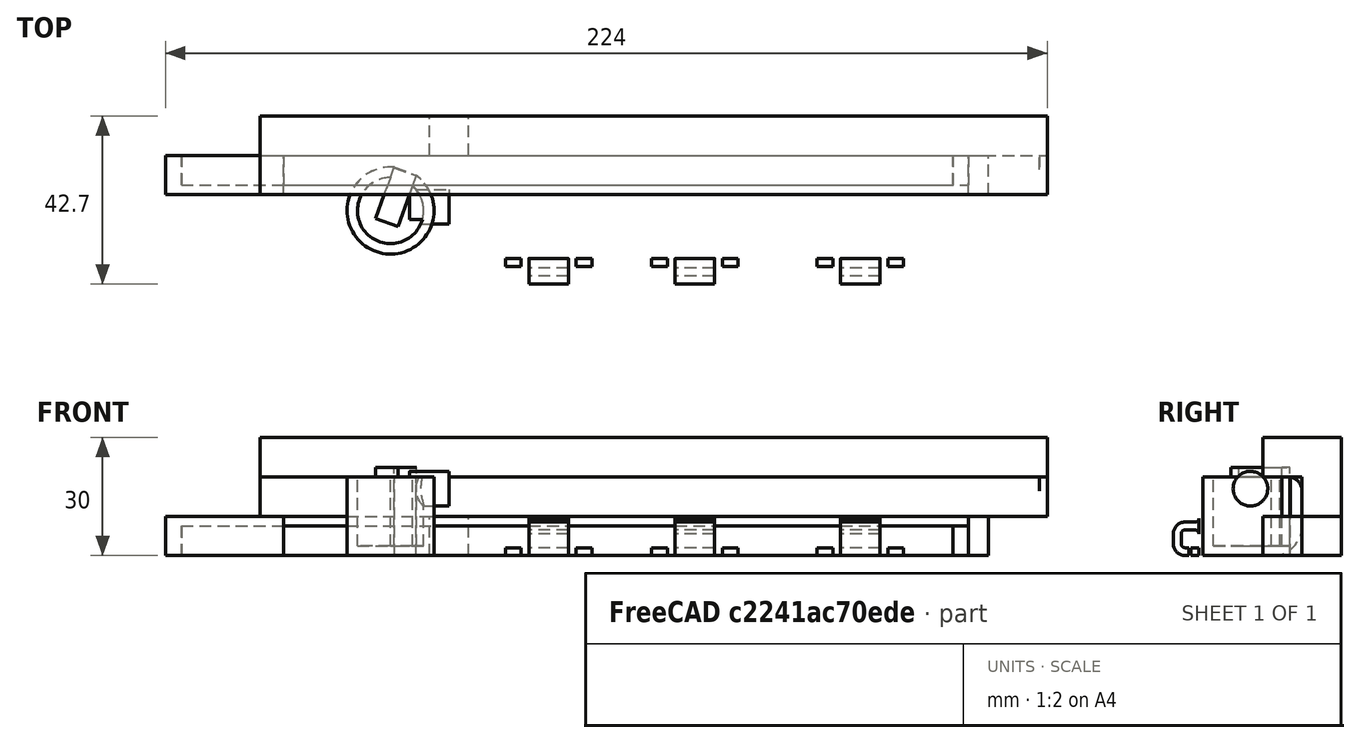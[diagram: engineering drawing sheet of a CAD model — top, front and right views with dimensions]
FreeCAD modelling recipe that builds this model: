
FCSTD DOCUMENT  (FreeCAD 0.19R0.19.2)
Label: v0_75
License: All rights reserved
LicenseURL: http://en.wikipedia.org/wiki/All_rights_reserved
objects: Part::Box×43, Part::Fillet×31, Part::MultiFuse×18, Part::Cut×13, Sketcher::SketchObject×11, Part::Extrusion×9, Part::Cylinder×6, App::MeasureDistance×5, Part::Revolution×1
note: 132 computed .brp shape members not serialized (recipe doc carries the construction recipe); baked Part::Feature solids carry a one-line shape summary decoded from their .brp

FEATURE [Sketcher::SketchObject] Sketch001
  FullyConstrained = true
  sketch-geometry (47):
    g0: Circle CenterX=-129.5 CenterY=-8 CenterZ=0 NormalX=0 NormalY=0 NormalZ=1 AngleXU=0 Radius=1
    g1: Circle CenterX=-129.5 CenterY=-3 CenterZ=0 NormalX=0 NormalY=0 NormalZ=1 AngleXU=0 Radius=1
    g2: Circle CenterX=-124.5 CenterY=-3 CenterZ=0 NormalX=0 NormalY=0 NormalZ=1 AngleXU=0 Radius=1
    g3: BSplineCurve PolesCount=3 KnotsCount=2 Degree=2 IsPeriodic=0
    g4: GeomPoint X=-129.5 Y=-8 Z=0
    g5: GeomPoint X=-124.5 Y=-3 Z=0
    g6: LineSegment StartX=18.6 StartY=-2.9 StartZ=0 EndX=23.6 EndY=-2.9 EndZ=0
    g7: ArcOfCircle CenterX=23.8 CenterY=-14.35 CenterZ=0 NormalX=0 NormalY=0 NormalZ=1 AngleXU=0 Radius=2.3 StartAngle=8e-16 EndAngle=1.5708
    g8: ArcOfCircle CenterX=23.8 CenterY=-18.1 CenterZ=0 NormalX=0 NormalY=0 NormalZ=1 AngleXU=0 Radius=2.3 StartAngle=4.71239 EndAngle=6.28319
    g9: LineSegment StartX=23.8 StartY=-20.4 StartZ=0 EndX=21.1 EndY=-20.4 EndZ=0
    g10: LineSegment StartX=21.1 StartY=-22.9 StartZ=0 EndX=21.1 EndY=-20.4 EndZ=0
    g11: LineSegment StartX=26.1 StartY=-14.35 StartZ=0 EndX=26.1 EndY=-18.1 EndZ=0
    g12: LineSegment StartX=18.6 StartY=-5.40742 StartZ=0 EndX=18.6 EndY=-2.9 EndZ=0
    g13: ArcOfCircle CenterX=18.8 CenterY=-8.1 CenterZ=0 NormalX=0 NormalY=0 NormalZ=1 AngleXU=0 Radius=2.7 StartAngle=1.64494 EndAngle=3.14159
    g14: ArcOfCircle CenterX=18.8 CenterY=-11.85 CenterZ=0 NormalX=0 NormalY=0 NormalZ=1 AngleXU=0 Radius=2.7 StartAngle=3.14159 EndAngle=4.71239
    g15: LineSegment StartX=16.1 StartY=-8.1 StartZ=0 EndX=16.1 EndY=-11.85 EndZ=0
    g16: LineSegment StartX=18.8 StartY=-14.55 StartZ=0 EndX=21.5 EndY=-14.55 EndZ=0
    g17: LineSegment StartX=21.5 StartY=-12.05 StartZ=0 EndX=21.5 EndY=-14.55 EndZ=0
    g18: LineSegment StartX=21.5 StartY=-12.05 StartZ=0 EndX=23.8 EndY=-12.05 EndZ=0
    g19: LineSegment StartX=16.1 StartY=-22.9 StartZ=0 EndX=21.1 EndY=-22.9 EndZ=0
    g20: LineSegment StartX=23.6 StartY=-2.9 StartZ=0 EndX=23.6 EndY=0 EndZ=0
    g21: LineSegment StartX=16.1 StartY=-22.9 StartZ=0 EndX=16.1 EndY=-26.2 EndZ=0
    g22: BSplineCurve PolesCount=3 KnotsCount=2 Degree=2 IsPeriodic=0
    g23: LineSegment StartX=2.6 StartY=-3 StartZ=0 EndX=-124.5 EndY=-3 EndZ=0
    g24: ArcOfCircle CenterX=-134.9 CenterY=-8.6 CenterZ=0 NormalX=0 NormalY=0 NormalZ=1 AngleXU=0 Radius=0.5 StartAngle=4.71238 EndAngle=6.28319
    g25: LineSegment StartX=-141.9 StartY=-9.1 StartZ=0 EndX=-134.9 EndY=-9.1 EndZ=0
    g26: LineSegment StartX=-141.9 StartY=-33.8 StartZ=0 EndX=-141.5 EndY=-33.8 EndZ=0
    g27: LineSegment StartX=-141.9 StartY=-9.1 StartZ=0 EndX=-141.9 EndY=-33.8 EndZ=0
    g28: LineSegment StartX=-134.4 StartY=-8.6 StartZ=0 EndX=-134.4 EndY=0 EndZ=0
    g29: LineSegment StartX=-134.4 StartY=0 StartZ=0 EndX=23.6 EndY=0 EndZ=0
    g30: LineSegment StartX=-133.5 StartY=-26.2 StartZ=0 EndX=16.1 EndY=-26.2 EndZ=0
    g31-g36: Circle x6 (B-spline internal-alignment scaffolding for g37; pole/knot coordinates omitted)
    g37: BSplineCurve PolesCount=6 KnotsCount=4 Degree=3 IsPeriodic=0
    g38-g41: GeomPoint x4 (B-spline internal-alignment scaffolding for g37; pole/knot coordinates omitted)
    g42: BSplineCurve PolesCount=3 KnotsCount=2 Degree=2 IsPeriodic=0
    g43: LineSegment StartX=-129.5 StartY=-8 StartZ=0 EndX=-129.5 EndY=-18.2 EndZ=0
    g44: BSplineCurve PolesCount=3 KnotsCount=2 Degree=2 IsPeriodic=0
    g45: LineSegment StartX=7.6 StartY=-8 StartZ=0 EndX=7.6 EndY=-18.2 EndZ=0
    g46: LineSegment StartX=2.6 StartY=-23.2 StartZ=0 EndX=-124.5 EndY=-23.2 EndZ=0
  constraints (87):
    c: Weight(g0) = 1
    c: Equal(g0,g1)
    c: Equal(g0,g2)
    c: InternalAlignment(g0,g3)
    c: InternalAlignment(g1,g3)
    c: InternalAlignment(g2,g3)
    c: InternalAlignment(g4,g3)
    c: InternalAlignment(g5,g3)
    c: Block(g3)
    c: Block(g8)
    c: Block(g7)
    c: Coincident(g9,g8)
    c: Horizontal(g9)
    c: Vertical(g10)
    c: Coincident(g10,g9)
    c: Coincident(g11,g7)
    c: Coincident(g11,g8)
    c: Vertical(g11)
    c: Vertical(g12)
    c: Block(g12)
    c: Coincident(g6,g12)
    c: Horizontal(g6)
    c: Block(g6)
    c: Coincident(g13,g12)
    c: Block(g14)
    c: Vertical(g15)
    c: Block(g15)
    c: Coincident(g16,g14)
    c: Horizontal(g16)
    c: Vertical(g17)
    c: Coincident(g17,g16)
    c: Block(g17)
    c: Coincident(g18,g7)
    c: Horizontal(g18)
    c: Block(g18)
    c: Coincident(g19,g10)
    c: Horizontal(g19)
    c: Block(g19)
    c: Block(g13)
    c: Coincident(g20,g6)
    c: Vertical(g20)
    c: Vertical(g21)
    c: Block(g21)
    c: Block(g22)
    c: Coincident(g23,g22)
    c: Coincident(g23,g3)
    c: Horizontal(g23)
    c: Block(g24)
    c: Coincident(g25,g24)
    c: Horizontal(g25)
    c: Horizontal(g26)
    c: Block(g26)
    c: Coincident(g27,g25)
    c: Coincident(g27,g26)
    c: Vertical(g27)
    c: Coincident(g28,g24)
    c: Vertical(g28)
    c: Coincident(g29,g28)
    c: Coincident(g29,g20)
    c: Horizontal(g29)
    c: Block(g29)
    c: Block(g25)
    c: Block(g28)
    c: Block(g27)
    c: Coincident(g30,g21)
    c: Horizontal(g30)
    c: Block(g30)
    c: Coincident(g37,g26)
    c: Weight(g31) = 1
    c: Equal(g31, g32-g36) x5
    c: Coincident(g37,g30)
    c: InternalAlignment(g31-g36 -> g37) x6
    c: InternalAlignment(g38-g41 -> g37) x4
    c: Block(g37)
    c: Block(g42)
    c: Coincident(g43,g3)
    c: Coincident(g43,g42)
    c: Vertical(g43)
    c: Distance(g43) = 10.2
    c: Block(g44)
    c: Coincident(g45,g22)
    c: Coincident(g45,g44)
    c: Vertical(g45)
    c: Distance(g45) = 10.2
    c: Coincident(g46,g44)
    c: Coincident(g46,g42)
    c: Horizontal(g46)
FEATURE [Part::Extrusion] Extrude001
  Base = -> Sketch001
  Dir = (0,0,1)
  DirMode = 2
  FaceMakerClass = Part::FaceMakerBullseye
  LengthFwd = 20
  LengthRev = 0
  Solid = true
  Symmetric = false
FEATURE [Sketcher::SketchObject] Sketch004
  FullyConstrained = true
  Placement = pos=(0,0,0) rot=(1,0,0;1.5708rad)
  sketch-geometry (12):
    g0: LineSegment StartX=15.75 StartY=2.5 StartZ=0 EndX=15.75 EndY=0 EndZ=0
    g1: Circle CenterX=15.75 CenterY=2.5 CenterZ=0 NormalX=0 NormalY=0 NormalZ=1 AngleXU=0 Radius=1
    g2: Circle CenterX=10.55 CenterY=2.5 CenterZ=0 NormalX=0 NormalY=0 NormalZ=1 AngleXU=0 Radius=1
    g3: Circle CenterX=10.55 CenterY=8 CenterZ=0 NormalX=0 NormalY=0 NormalZ=1 AngleXU=0 Radius=1
    g4: BSplineCurve PolesCount=3 KnotsCount=2 Degree=2 IsPeriodic=0
    g5: GeomPoint X=15.75 Y=2.5 Z=0
    g6: GeomPoint X=10.55 Y=8 Z=0
    g7: LineSegment StartX=1.9 StartY=8 StartZ=0 EndX=10.55 EndY=8 EndZ=0
    g8: LineSegment StartX=1.9 StartY=-2.4 StartZ=0 EndX=1.9 EndY=8 EndZ=0
    g9: LineSegment StartX=3.30092 StartY=-2.4 StartZ=0 EndX=3.30092 EndY=0 EndZ=0
    g10: LineSegment StartX=15.75 StartY=0 StartZ=0 EndX=3.30092 EndY=0 EndZ=0
    g11: LineSegment StartX=3.30092 StartY=-2.4 StartZ=0 EndX=1.9 EndY=-2.4 EndZ=0
  constraints (26):
    c: Vertical(g0)
    c: Distance(g0) = 2.5
    c: Coincident(g4,g0)
    c: Weight(g1) = 1
    c: Equal(g1,g2)
    c: Equal(g1,g3)
    c: InternalAlignment(g1,g4)
    c: InternalAlignment(g2,g4)
    c: InternalAlignment(g3,g4)
    c: InternalAlignment(g5,g4)
    c: InternalAlignment(g6,g4)
    c: Block(g4)
    c: Coincident(g7,g4)
    c: Horizontal(g7)
    c: Vertical(g8)
    c: Coincident(g8,g7)
    c: Block(g8)
    c: Vertical(g9)
    c: Coincident(g10,g0)
    c: PointOnObject(g10,g-1)
    c: Horizontal(g10)
    c: Coincident(g10,g9)
    c: Block(g9)
    c: Coincident(g11,g9)
    c: Coincident(g11,g8)
    c: Horizontal(g11)
FEATURE [Part::Revolution] Revolve  label="mainScrewStandRevolve"
  Angle = 360
  Axis = (0,0,1)
  Base = (0,0,0)
  FaceMakerClass = Part::FaceMakerBullseye
  Placement = pos=(-101.95,-15.3,0) rot=(0,0,1;0rad)
  Solid = true
  Source = -> Sketch004
  Symmetric = false
FEATURE [Sketcher::SketchObject] Sketch044
  FullyConstrained = true
  MapMode = 4
  Placement = pos=(0,0,0) rot=(0.57735,0.57735,0.57735;2.0944rad)
  sketch-geometry (14):
    g0: LineSegment StartX=6.08745 StartY=-4.11588 StartZ=0 EndX=6.08745 EndY=-2.11589 EndZ=0
    g1: LineSegment StartX=8.08745 StartY=1.38411 StartZ=0 EndX=8.08745 EndY=-1.11589 EndZ=0
    g2: ArcOfCircle CenterX=7.08745 CenterY=-1.11589 CenterZ=0 NormalX=0 NormalY=0 NormalZ=1 AngleXU=0 Radius=1 StartAngle=4.71239 EndAngle=6.28319
    g3: LineSegment StartX=6.08745 StartY=-2.11589 StartZ=0 EndX=7.08745 EndY=-2.11589 EndZ=0
    g4: LineSegment StartX=6.08745 StartY=-4.11588 StartZ=0 EndX=7.08745 EndY=-4.11588 EndZ=0
    g5: ArcOfCircle CenterX=7.08745 CenterY=-1.11589 CenterZ=0 NormalX=0 NormalY=0 NormalZ=1 AngleXU=0 Radius=3 StartAngle=4.71239 EndAngle=6.28319
    g6: ArcOfCircle CenterX=7.08745 CenterY=1.38411 CenterZ=0 NormalX=0 NormalY=0 NormalZ=1 AngleXU=0 Radius=1 StartAngle=5.35e-14 EndAngle=1.5708
    g7: LineSegment StartX=10.0875 StartY=-1.11588 StartZ=0 EndX=10.0875 EndY=1.38411 EndZ=0
    g8: ArcOfCircle CenterX=7.08745 CenterY=1.38411 CenterZ=0 NormalX=0 NormalY=0 NormalZ=1 AngleXU=0 Radius=3 StartAngle=3.57e-14 EndAngle=1.5708
    g9: ArcOfCircle CenterX=4.58745 CenterY=1.38412 CenterZ=0 NormalX=0 NormalY=0 NormalZ=1 AngleXU=0 Radius=1 StartAngle=1.57081 EndAngle=3.14159
    g10: LineSegment StartX=4.58744 StartY=2.38411 StartZ=0 EndX=7.08745 EndY=2.38411 EndZ=0
    g11: LineSegment StartX=4.58745 StartY=4.38411 StartZ=0 EndX=7.08745 EndY=4.38411 EndZ=0
    g12: ArcOfCircle CenterX=4.58745 CenterY=5.38411 CenterZ=0 NormalX=0 NormalY=0 NormalZ=1 AngleXU=0 Radius=1 StartAngle=3.14159 EndAngle=4.71239
    g13: LineSegment StartX=3.58745 StartY=5.38411 StartZ=0 EndX=3.58745 EndY=1.38411 EndZ=0
  constraints (33):
    c: Vertical(g0)
    c: Block(g0)
    c: Block(g1)
    c: Coincident(g2,g1)
    c: Coincident(g3,g0)
    c: Coincident(g3,g2)
    c: Horizontal(g3)
    c: Block(g2)
    c: Coincident(g4,g0)
    c: Horizontal(g4)
    c: Coincident(g5,g2)
    c: Block(g5)
    c: Block(g4)
    c: Coincident(g6,g1)
    c: Block(g6)
    c: Coincident(g7,g5)
    c: Vertical(g7)
    c: Coincident(g8,g6)
    c: Block(g8)
    c: Block(g7)
    c: Coincident(g10,g9)
    c: Coincident(g10,g6)
    c: Horizontal(g10)
    c: Block(g10)
    c: Block(g9)
    c: Coincident(g11,g8)
    c: Horizontal(g11)
    c: Block(g12)
    c: Block(g11)
    c: Coincident(g13,g12)
    c: Coincident(g13,g9)
    c: Vertical(g13)
    c: Tangent(g13,g9)
FEATURE [Sketcher::SketchObject] Sketch045
  FullyConstrained = true
  MapMode = 4
  Placement = pos=(0,0,0) rot=(0.57735,0.57735,0.57735;2.0944rad)
  sketch-geometry (14):
    g0: LineSegment StartX=6.08745 StartY=-4.11588 StartZ=0 EndX=6.08745 EndY=-2.11589 EndZ=0
    g1: LineSegment StartX=8.08745 StartY=1.38411 StartZ=0 EndX=8.08745 EndY=-1.11589 EndZ=0
    g2: ArcOfCircle CenterX=7.08745 CenterY=-1.11589 CenterZ=0 NormalX=0 NormalY=0 NormalZ=1 AngleXU=0 Radius=1 StartAngle=4.71239 EndAngle=6.28319
    g3: LineSegment StartX=6.08745 StartY=-2.11589 StartZ=0 EndX=7.08745 EndY=-2.11589 EndZ=0
    g4: LineSegment StartX=6.08745 StartY=-4.11588 StartZ=0 EndX=7.08745 EndY=-4.11588 EndZ=0
    g5: ArcOfCircle CenterX=7.08745 CenterY=-1.11589 CenterZ=0 NormalX=0 NormalY=0 NormalZ=1 AngleXU=0 Radius=3 StartAngle=4.71239 EndAngle=6.28319
    g6: ArcOfCircle CenterX=7.08745 CenterY=1.38411 CenterZ=0 NormalX=0 NormalY=0 NormalZ=1 AngleXU=0 Radius=1 StartAngle=5.35e-14 EndAngle=1.5708
    g7: LineSegment StartX=10.0875 StartY=-1.11588 StartZ=0 EndX=10.0875 EndY=1.38411 EndZ=0
    g8: ArcOfCircle CenterX=7.08745 CenterY=1.38411 CenterZ=0 NormalX=0 NormalY=0 NormalZ=1 AngleXU=0 Radius=3 StartAngle=3.57e-14 EndAngle=1.5708
    g9: ArcOfCircle CenterX=4.58745 CenterY=1.38412 CenterZ=0 NormalX=0 NormalY=0 NormalZ=1 AngleXU=0 Radius=1 StartAngle=1.57081 EndAngle=3.14159
    g10: LineSegment StartX=4.58744 StartY=2.38411 StartZ=0 EndX=7.08745 EndY=2.38411 EndZ=0
    g11: LineSegment StartX=4.58745 StartY=4.38411 StartZ=0 EndX=7.08745 EndY=4.38411 EndZ=0
    g12: ArcOfCircle CenterX=4.58745 CenterY=5.38411 CenterZ=0 NormalX=0 NormalY=0 NormalZ=1 AngleXU=0 Radius=1 StartAngle=3.14159 EndAngle=4.71239
    g13: LineSegment StartX=3.58745 StartY=5.38411 StartZ=0 EndX=3.58745 EndY=1.38411 EndZ=0
  constraints (33):
    c: Vertical(g0)
    c: Block(g0)
    c: Block(g1)
    c: Coincident(g2,g1)
    c: Coincident(g3,g0)
    c: Coincident(g3,g2)
    c: Horizontal(g3)
    c: Block(g2)
    c: Coincident(g4,g0)
    c: Horizontal(g4)
    c: Coincident(g5,g2)
    c: Block(g5)
    c: Block(g4)
    c: Coincident(g6,g1)
    c: Block(g6)
    c: Coincident(g7,g5)
    c: Vertical(g7)
    c: Coincident(g8,g6)
    c: Block(g8)
    c: Block(g7)
    c: Coincident(g10,g9)
    c: Coincident(g10,g6)
    c: Horizontal(g10)
    c: Block(g10)
    c: Block(g9)
    c: Coincident(g11,g8)
    c: Horizontal(g11)
    c: Block(g12)
    c: Block(g11)
    c: Coincident(g13,g12)
    c: Coincident(g13,g9)
    c: Vertical(g13)
    c: Tangent(g13,g9)
FEATURE [Part::Extrusion] Extrude040
  Base = -> Sketch045
  Dir = (1,0,0)
  DirMode = 2
  FaceMakerClass = Part::FaceMakerBullseye
  LengthFwd = 10
  LengthRev = 0
  Placement = pos=(-71.7,-22.61,4.115) rot=(0,0,1;3.14159rad)
  Solid = true
  Symmetric = false
FEATURE [Part::Box] Box017  label="Cube017"
  AttacherType = Attacher::AttachEngine3D
  Height = 2
  Length = 2
  Placement = pos=(-85.7,-21.3,0) rot=(0,0,1;0rad)
  Width = 2
FEATURE [Part::Box] Box018  label="Cube018"
  AttacherType = Attacher::AttachEngine3D
  Height = 2
  Length = 2
  Placement = pos=(-87.7,-21.3,0) rot=(0,0,1;0rad)
  Width = 2
FEATURE [Part::MultiFuse] Fusion
  Placement = pos=(0,-6.9,0) rot=(0,0,1;0rad)
  Shapes = -> [Box017,Box018]
FEATURE [Part::Box] Box  label="Cube"
  AttacherType = Attacher::AttachEngine3D
  Height = 10
  Length = 10
  Placement = pos=(-107,0,0) rot=(0,0,1;0rad)
  Width = 10
FEATURE [Sketcher::SketchObject] Sketch046
  FullyConstrained = true
  MapMode = 4
  Placement = pos=(0,0,0) rot=(0.57735,0.57735,0.57735;2.0944rad)
  sketch-geometry (14):
    g0: LineSegment StartX=6.08745 StartY=-4.11588 StartZ=0 EndX=6.08745 EndY=-2.11589 EndZ=0
    g1: LineSegment StartX=8.08745 StartY=1.38411 StartZ=0 EndX=8.08745 EndY=-1.11589 EndZ=0
    g2: ArcOfCircle CenterX=7.08745 CenterY=-1.11589 CenterZ=0 NormalX=0 NormalY=0 NormalZ=1 AngleXU=0 Radius=1 StartAngle=4.71239 EndAngle=6.28319
    g3: LineSegment StartX=6.08745 StartY=-2.11589 StartZ=0 EndX=7.08745 EndY=-2.11589 EndZ=0
    g4: LineSegment StartX=6.08745 StartY=-4.11588 StartZ=0 EndX=7.08745 EndY=-4.11588 EndZ=0
    g5: ArcOfCircle CenterX=7.08745 CenterY=-1.11589 CenterZ=0 NormalX=0 NormalY=0 NormalZ=1 AngleXU=0 Radius=3 StartAngle=4.71239 EndAngle=6.28319
    g6: ArcOfCircle CenterX=7.08745 CenterY=1.38411 CenterZ=0 NormalX=0 NormalY=0 NormalZ=1 AngleXU=0 Radius=1 StartAngle=5.35e-14 EndAngle=1.5708
    g7: LineSegment StartX=10.0875 StartY=-1.11588 StartZ=0 EndX=10.0875 EndY=1.38411 EndZ=0
    g8: ArcOfCircle CenterX=7.08745 CenterY=1.38411 CenterZ=0 NormalX=0 NormalY=0 NormalZ=1 AngleXU=0 Radius=3 StartAngle=3.57e-14 EndAngle=1.5708
    g9: ArcOfCircle CenterX=4.58745 CenterY=1.38412 CenterZ=0 NormalX=0 NormalY=0 NormalZ=1 AngleXU=0 Radius=1 StartAngle=1.57081 EndAngle=3.14159
    g10: LineSegment StartX=4.58744 StartY=2.38411 StartZ=0 EndX=7.08745 EndY=2.38411 EndZ=0
    g11: LineSegment StartX=4.58745 StartY=4.38411 StartZ=0 EndX=7.08745 EndY=4.38411 EndZ=0
    g12: ArcOfCircle CenterX=4.58745 CenterY=5.38411 CenterZ=0 NormalX=0 NormalY=0 NormalZ=1 AngleXU=0 Radius=1 StartAngle=3.14159 EndAngle=4.71239
    g13: LineSegment StartX=3.58745 StartY=5.38411 StartZ=0 EndX=3.58745 EndY=1.38411 EndZ=0
  constraints (33):
    c: Vertical(g0)
    c: Block(g0)
    c: Block(g1)
    c: Coincident(g2,g1)
    c: Coincident(g3,g0)
    c: Coincident(g3,g2)
    c: Horizontal(g3)
    c: Block(g2)
    c: Coincident(g4,g0)
    c: Horizontal(g4)
    c: Coincident(g5,g2)
    c: Block(g5)
    c: Block(g4)
    c: Coincident(g6,g1)
    c: Block(g6)
    c: Coincident(g7,g5)
    c: Vertical(g7)
    c: Coincident(g8,g6)
    c: Block(g8)
    c: Block(g7)
    c: Coincident(g10,g9)
    c: Coincident(g10,g6)
    c: Horizontal(g10)
    c: Block(g10)
    c: Block(g9)
    c: Coincident(g11,g8)
    c: Horizontal(g11)
    c: Block(g12)
    c: Block(g11)
    c: Coincident(g13,g12)
    c: Coincident(g13,g9)
    c: Vertical(g13)
    c: Tangent(g13,g9)
FEATURE [Part::Extrusion] Extrude041
  Base = -> Sketch046
  Dir = (1,0,0)
  DirMode = 2
  FaceMakerClass = Part::FaceMakerBullseye
  LengthFwd = 10
  LengthRev = 0
  Placement = pos=(7.5,-22.61,4.115) rot=(0,0,1;3.14159rad)
  Solid = true
  Symmetric = false
FEATURE [Part::Box] Box042  label="Cube042"
  AttacherType = Attacher::AttachEngine3D
  Height = 2
  Length = 2
  Placement = pos=(-87.7,-21.3,0) rot=(0,0,1;0rad)
  Width = 2
FEATURE [Part::Box] Box043  label="Cube043"
  AttacherType = Attacher::AttachEngine3D
  Height = 2
  Length = 2
  Placement = pos=(-85.7,-21.3,0) rot=(0,0,1;0rad)
  Width = 2
FEATURE [Part::MultiFuse] Fusion019
  Placement = pos=(37.15,-6.9,0) rot=(0,0,1;0rad)
  Shapes = -> [Box043,Box042]
FEATURE [Part::Box] Box005  label="Cube005"
  AttacherType = Attacher::AttachEngine3D
  Height = 10
  Length = 198
  Placement = pos=(-30,0,0) rot=(0,0,1;0rad)
  Width = 10
FEATURE [Part::Box] Box004  label="Cube004"
  AttacherType = Attacher::AttachEngine3D
  Height = 10
  Length = 200
  Placement = pos=(-30,0,0) rot=(0,0,1;0rad)
  Width = 10
FEATURE [Part::Fillet] Fillet020
  Base = -> Box004
  Edges = 1 edges r=3.6: [Edge12]
FEATURE [Sketcher::SketchObject] Sketch
  FullyConstrained = true
  sketch-geometry (35):
    g0: Circle CenterX=-101.95 CenterY=-14.3 CenterZ=0 NormalX=0 NormalY=0 NormalZ=1 AngleXU=0 Radius=3.25
    g1: LineSegment StartX=16.1 StartY=-26.2 StartZ=0 EndX=16.1 EndY=-22.9 EndZ=0
    g2: ArcOfCircle CenterX=23.8 CenterY=-14.35 CenterZ=0 NormalX=0 NormalY=0 NormalZ=1 AngleXU=0 Radius=2.3 StartAngle=8e-16 EndAngle=1.5708
    g3: LineSegment StartX=18.6 StartY=-5.40742 StartZ=0 EndX=18.6 EndY=-2.9 EndZ=0
    g4: LineSegment StartX=18.6 StartY=-2.9 StartZ=0 EndX=23.6 EndY=-2.9 EndZ=0
    g5: LineSegment StartX=23.6 StartY=-2.9 StartZ=0 EndX=23.6 EndY=2.58e-14 EndZ=0
    g6: LineSegment StartX=18.8 StartY=-14.55 StartZ=0 EndX=21.5 EndY=-14.55 EndZ=0
    g7: LineSegment StartX=21.5 StartY=-12.05 StartZ=0 EndX=21.5 EndY=-14.55 EndZ=0
    g8: LineSegment StartX=21.5 StartY=-12.05 StartZ=0 EndX=23.8 EndY=-12.05 EndZ=0
    g9: ArcOfCircle CenterX=23.8 CenterY=-18.1 CenterZ=0 NormalX=0 NormalY=0 NormalZ=1 AngleXU=0 Radius=2.3 StartAngle=4.71239 EndAngle=6.28319
    g10: LineSegment StartX=23.8 StartY=-20.4 StartZ=0 EndX=21.1 EndY=-20.4 EndZ=0
    g11: LineSegment StartX=26.1 StartY=-14.35 StartZ=0 EndX=26.1 EndY=-18.1 EndZ=0
    g12: ArcOfCircle CenterX=18.8 CenterY=-8.1 CenterZ=0 NormalX=0 NormalY=0 NormalZ=1 AngleXU=0 Radius=2.7 StartAngle=1.64494 EndAngle=3.14159
    g13: ArcOfCircle CenterX=18.8 CenterY=-11.85 CenterZ=0 NormalX=0 NormalY=0 NormalZ=1 AngleXU=0 Radius=2.7 StartAngle=3.14159 EndAngle=4.71239
    g14: LineSegment StartX=16.1 StartY=-8.1 StartZ=0 EndX=16.1 EndY=-11.85 EndZ=0
    g15: LineSegment StartX=21.1 StartY=-22.9 StartZ=0 EndX=21.1 EndY=-20.4 EndZ=0
    g16: LineSegment StartX=16.1 StartY=-22.9 StartZ=0 EndX=21.1 EndY=-22.9 EndZ=0
    g17: LineSegment StartX=23.6 StartY=2.58e-14 StartZ=0 EndX=-134.4 EndY=2.58e-14 EndZ=0
    g18: LineSegment StartX=-134.4 StartY=2.59e-14 StartZ=0 EndX=-134.4 EndY=-8.6 EndZ=0
    g19: ArcOfCircle CenterX=-134.9 CenterY=-8.6 CenterZ=0 NormalX=0 NormalY=0 NormalZ=1 AngleXU=0 Radius=0.5 StartAngle=4.71238 EndAngle=6.28319
    g20: LineSegment StartX=-134.9 StartY=-9.1 StartZ=0 EndX=-141.9 EndY=-9.1 EndZ=0
    g21: LineSegment StartX=-141.9 StartY=-9.1 StartZ=0 EndX=-141.9 EndY=-33.8 EndZ=0
    g22: LineSegment StartX=-141.9 StartY=-33.8 StartZ=0 EndX=-141.5 EndY=-33.8 EndZ=0
    g23: LineSegment StartX=-133.5 StartY=-26.2 StartZ=0 EndX=16.1 EndY=-26.2 EndZ=0
    g24-g29: Circle x6 (B-spline internal-alignment scaffolding for g30; pole/knot coordinates omitted)
    g30: BSplineCurve PolesCount=6 KnotsCount=4 Degree=3 IsPeriodic=0
    g31-g34: GeomPoint x4 (B-spline internal-alignment scaffolding for g30; pole/knot coordinates omitted)
  constraints (61):
    c: Block(g0)
    c: Vertical(g1)
    c: Distance(g1) = 3.3
    c: Block(g9)
    c: Block(g2)
    c: Coincident(g10,g9)
    c: Horizontal(g10)
    c: Vertical(g15)
    c: Coincident(g15,g10)
    c: Coincident(g11,g2)
    c: Coincident(g11,g9)
    c: Vertical(g11)
    c: Vertical(g3)
    c: Block(g3)
    c: Coincident(g4,g3)
    c: Horizontal(g4)
    c: Vertical(g5)
    c: Block(g5)
    c: Block(g4)
    c: Coincident(g12,g3)
    c: Block(g13)
    c: Coincident(g14,g12)
    c: Vertical(g14)
    c: Block(g14)
    c: Coincident(g6,g13)
    c: Horizontal(g6)
    c: Vertical(g7)
    c: Coincident(g7,g6)
    c: Block(g7)
    c: Coincident(g8,g2)
    c: Horizontal(g8)
    c: Block(g8)
    c: Coincident(g16,g15)
    c: Horizontal(g16)
    c: Block(g16)
    c: Block(g12)
    c: Coincident(g16,g1)
    c: Coincident(g17,g5)
    c: Horizontal(g17)
    c: Vertical(g18)
    c: Horizontal(g20)
    c: Coincident(g19,g18)
    c: Coincident(g19,g20)
    c: Block(g19)
    c: Coincident(g21,g20)
    c: Vertical(g21)
    c: Block(g21)
    c: Coincident(g22,g21)
    c: Horizontal(g22)
    c: Block(g22)
    c: Block(g18)
    c: Coincident(g18,g17)
    c: Coincident(g23,g1)
    c: Horizontal(g23)
    c: Distance(g23) = 149.6
    c: Coincident(g30,g22)
    c: Weight(g24) = 1
    c: Equal(g24, g25-g29) x5
    c: InternalAlignment(g24-g29 -> g30) x6
    c: InternalAlignment(g31-g34 -> g30) x4
    c: Block(g30)
FEATURE [Part::Extrusion] Extrude
  Base = -> Sketch
  Dir = (0,0,1)
  DirMode = 2
  FaceMakerClass = Part::FaceMakerBullseye
  LengthFwd = 2.4
  LengthRev = 0
  Solid = true
  Symmetric = false
FEATURE [Part::Box] Box051  label="Cube051"
  AttacherType = Attacher::AttachEngine3D
  Height = 10
  Length = 198
  Placement = pos=(-30,0,0) rot=(0,0,1;0rad)
  Width = 10
FEATURE [Part::Box] Box052  label="Cube052"
  AttacherType = Attacher::AttachEngine3D
  Height = 5
  Length = 200
  Placement = pos=(-30,6.4,10) rot=(1,0,0;0rad)
  Width = 5
FEATURE [Part::Box] Box053  label="Cube053"
  AttacherType = Attacher::AttachEngine3D
  Height = 5
  Length = 200
  Placement = pos=(-30,6.4,10) rot=(1,0,0;0.872665rad)
  Width = 5
FEATURE [Part::Box] Box054  label="Cube054"
  AttacherType = Attacher::AttachEngine3D
  Height = 10
  Length = 200
  Placement = pos=(-30,0,0) rot=(0,0,1;0rad)
  Width = 10
FEATURE [Part::Fillet] Fillet021
  Base = -> Box054
  Edges = 1 edges r=3.6: [Edge12]
FEATURE [Part::Cut] Cut015
  Base = -> Box051
  Tool = -> Fillet021
FEATURE [Part::MultiFuse] Fusion033  label="removeFromMainFusion014"
  Placement = pos=(-120,-10,10) rot=(0,0,1;0rad)
  Shapes = -> [Box053,Box052,Cut015]
FEATURE [Part::Box] Box055  label="Cube055"
  AttacherType = Attacher::AttachEngine3D
  Height = 10
  Length = 190
  Placement = pos=(-30,0,0) rot=(0,0,1;0rad)
  Width = 10
FEATURE [Part::Box] Box056  label="Cube056"
  AttacherType = Attacher::AttachEngine3D
  Height = 10
  Length = 190
  Placement = pos=(-35,0,0) rot=(0,0,1;0rad)
  Width = 10
FEATURE [Part::Fillet] Fillet022
  Base = -> Box055
  Edges = 1 edges r=7.5: [Edge11]
FEATURE [Part::Cut] Cut014  label="filletMain001"
  Base = -> Box056
  Placement = pos=(-120,-10,0) rot=(0,0,1;0rad)
  Tool = -> Fillet022
FEATURE [Part::MultiFuse] Fusion032  label="removeFromMain001"
  Shapes = -> [Fusion033,Cut014]
FEATURE [Part::Cut] Cut017
  Base = -> Extrude
  Tool = -> Fusion032
FEATURE [Part::Box] Box063  label="Cube063"
  AttacherType = Attacher::AttachEngine3D
  Height = 10
  Length = 198
  Placement = pos=(-30,0,0) rot=(0,0,1;0rad)
  Width = 10
FEATURE [Part::Box] Box064  label="Cube064"
  AttacherType = Attacher::AttachEngine3D
  Height = 5
  Length = 200
  Placement = pos=(-30,6.4,10) rot=(1,0,0;0rad)
  Width = 5
FEATURE [Part::Box] Box065  label="Cube065"
  AttacherType = Attacher::AttachEngine3D
  Height = 5
  Length = 200
  Placement = pos=(-30,6.4,10) rot=(1,0,0;0.872665rad)
  Width = 5
FEATURE [Part::Box] Box066  label="Cube066"
  AttacherType = Attacher::AttachEngine3D
  Height = 10
  Length = 200
  Placement = pos=(-30,0,0) rot=(0,0,1;0rad)
  Width = 10
FEATURE [Part::Fillet] Fillet023
  Base = -> Box066
  Edges = 1 edges r=3.6: [Edge12]
FEATURE [Part::Cut] Cut018
  Base = -> Box063
  Tool = -> Fillet023
FEATURE [Part::MultiFuse] Fusion035  label="removeFromMainFusion015"
  Placement = pos=(-120,-10,10) rot=(0,0,1;0rad)
  Shapes = -> [Box065,Box064,Cut018]
FEATURE [Part::Box] Box067  label="Cube067"
  AttacherType = Attacher::AttachEngine3D
  Height = 10
  Length = 190
  Placement = pos=(-30,0,0) rot=(0,0,1;0rad)
  Width = 10
FEATURE [Part::Fillet] Fillet024
  Base = -> Box067
  Edges = 1 edges r=7.5: [Edge11]
FEATURE [Part::Box] Box068  label="Cube068"
  AttacherType = Attacher::AttachEngine3D
  Height = 10
  Length = 190
  Placement = pos=(-35,0,0) rot=(0,0,1;0rad)
  Width = 10
FEATURE [Part::Cut] Cut019  label="filletMain002"
  Base = -> Box068
  Placement = pos=(-120,-10,0) rot=(0,0,1;0rad)
  Tool = -> Fillet024
FEATURE [Part::MultiFuse] Fusion036  label="removeFromMain002"
  Shapes = -> [Fusion035,Cut019]
FEATURE [Part::Box] Box069  label="Cube069"
  AttacherType = Attacher::AttachEngine3D
  Height = 20
  Length = 10
  Placement = pos=(-144.4,-8,0) rot=(0,0,1;0rad)
  Width = 10
FEATURE [Part::Box] Box070  label="Cube070"
  AttacherType = Attacher::AttachEngine3D
  Height = 20
  Length = 30
  Placement = pos=(-120,0,0) rot=(0,0,1;0rad)
  Width = 20
FEATURE [Part::MultiFuse] Fusion037  label="removeFromIntegrityIncreaserFusion037"
  Shapes = -> [Box069,Box070,Fusion036]
FEATURE [Sketcher::SketchObject] Sketch047
  FullyConstrained = true
  sketch-geometry (4):
    g0: LineSegment StartX=20.5 StartY=-1.82002 StartZ=0 EndX=20.5 EndY=-36 EndZ=0
    g1: LineSegment StartX=32.7 StartY=-36 StartZ=0 EndX=32.7 EndY=-1.82002 EndZ=0
    g2: LineSegment StartX=20.5 StartY=-1.82002 StartZ=0 EndX=32.7 EndY=-1.82002 EndZ=0
    g3: LineSegment StartX=20.5 StartY=-36 StartZ=0 EndX=32.7 EndY=-36 EndZ=0
  constraints (12):
    c: Vertical(g0)
    c: Distance(g0) = 34.18
    c: Vertical(g1)
    c: Block(g0)
    c: Coincident(g2,g0)
    c: Horizontal(g2)
    c: Coincident(g2,g1)
    c: Block(g2)
    c: Block(g1)
    c: Coincident(g3,g0)
    c: Coincident(g3,g1)
    c: Horizontal(g3)
FEATURE [Part::Cut] Cut021
  Base = -> Box005
  Tool = -> Fillet020
FEATURE [Part::Box] Box073  label="Cube073"
  AttacherType = Attacher::AttachEngine3D
  Height = 10
  Length = 200
  Placement = pos=(-30,10,0) rot=(0,0,1;0rad)
  Width = 10
FEATURE [Part::Box] Box074  label="Cube074"
  AttacherType = Attacher::AttachEngine3D
  Height = 10
  Length = 200
  Placement = pos=(-30,0,10) rot=(0,0,1;0rad)
  Width = 10
FEATURE [Part::Box] Box075  label="Cube075"
  AttacherType = Attacher::AttachEngine3D
  Height = 10
  Length = 200
  Placement = pos=(-30,10,10) rot=(0,0,1;0rad)
  Width = 10
FEATURE [Part::MultiFuse] Fusion043  label="removeFromMainFusion043"
  Placement = pos=(-120,-10,10) rot=(0,0,1;0rad)
  Shapes = -> [Cut021,Box074,Box073,Box075]
FEATURE [Part::Box] Box076  label="Cube076"
  AttacherType = Attacher::AttachEngine3D
  Height = 10
  Length = 200
  Placement = pos=(-160,0,0) rot=(0,0,1;0rad)
  Width = 10
FEATURE [Part::Box] Box077  label="Cube077"
  AttacherType = Attacher::AttachEngine3D
  Height = 10
  Length = 170
  Placement = pos=(-130,0,0) rot=(0,0,1;0rad)
  Width = 10
FEATURE [Part::Fillet] Fillet028
  Base = -> Box077
  Edges = 1 edges r=7.5: [Edge11]
FEATURE [Part::Cut] Cut024
  Base = -> Box076
  Placement = pos=(-14,-10,0) rot=(0,0,1;0rad)
  Tool = -> Fillet028
FEATURE [Part::Box] Box078  label="Cube078"
  AttacherType = Attacher::AttachEngine3D
  Height = 10
  Length = 200
  Width = 10
FEATURE [Part::Box] Box079  label="Cube079"
  AttacherType = Attacher::AttachEngine3D
  Height = 10
  Length = 205
  Placement = pos=(10,0,0) rot=(0,0,1;0rad)
  Width = 10
FEATURE [Part::Fillet] Fillet029
  Base = -> Box078
  Edges = 1 edges r=7.5: [Edge11]
  Placement = pos=(10,0,0) rot=(0,0,1;0rad)
FEATURE [Part::Cut] Cut025  label="removeFromMainCut025"
  Base = -> Box079
  Placement = pos=(-180,-10,0) rot=(0,0,1;0rad)
  Tool = -> Fillet029
FEATURE [Part::Cylinder] Cylinder001
  Angle = 360
  AttacherType = Attacher::AttachEngine3D
  Height = 10
  Placement = pos=(-36.2,-2,12) rot=(0,1,0;1.5708rad)
  Radius = 2
FEATURE [App::MeasureDistance] Distance  label="Distance: 4.02 mm"
  Distance = 4.02
  P1 = (-33.21,5.8978,9.90268)
  P2 = (-29.19,5.8978,9.90268)
FEATURE [Part::Fillet] Fillet030
  Base = -> Cylinder001
  Edges = 1 edges r=1.8: [Edge3]
FEATURE [Part::Fillet] Fillet031
  Base = -> Fillet030
  Edges = 1 edges r=1.8: [Edge2]
FEATURE [Part::Cylinder] Cylinder003
  Angle = 360
  AttacherType = Attacher::AttachEngine3D
  Height = 10
  Placement = pos=(-36.2,-2,12) rot=(0,1,0;1.5708rad)
  Radius = 2
FEATURE [Part::Fillet] Fillet035
  Base = -> Cylinder003
  Edges = 1 edges r=1.8: [Edge3]
FEATURE [Part::Fillet] Fillet036
  Base = -> Fillet035
  Edges = 1 edges r=1.8: [Edge2]
  Placement = pos=(-12.8,0,0) rot=(0,0,1;0rad)
FEATURE [Part::Cylinder] Cylinder004
  Angle = 360
  AttacherType = Attacher::AttachEngine3D
  Height = 10
  Placement = pos=(-36.2,-2,12) rot=(0,1,0;1.5708rad)
  Radius = 2
FEATURE [Part::Fillet] Fillet038
  Base = -> Cylinder004
  Edges = 1 edges r=1.8: [Edge3]
FEATURE [Part::Fillet] Fillet037
  Base = -> Fillet038
  Edges = 1 edges r=1.8: [Edge2]
  Placement = pos=(-6.4,0,0) rot=(0,0,1;0rad)
FEATURE [Sketcher::SketchObject] Sketch048
  FullyConstrained = true
  sketch-geometry (4):
    g0: LineSegment StartX=-5.1 StartY=-34.18 StartZ=0 EndX=5.1 EndY=-34.18 EndZ=0
    g1: LineSegment StartX=-5.1 StartY=-3.93167e-07 StartZ=0 EndX=-5.1 EndY=-34.18 EndZ=0
    g2: LineSegment StartX=5.1 StartY=-34.18 StartZ=0 EndX=5.1 EndY=-3.93167e-07 EndZ=0
    g3: LineSegment StartX=-5.1 StartY=-3.93167e-07 StartZ=0 EndX=5.1 EndY=-3.93167e-07 EndZ=0
  constraints (10):
    c: Horizontal(g0)
    c: Block(g0)
    c: Coincident(g1,g0)
    c: Vertical(g1)
    c: Coincident(g2,g0)
    c: Vertical(g2)
    c: Coincident(g3,g1)
    c: Coincident(g3,g2)
    c: Horizontal(g3)
    c: Block(g3)
FEATURE [Part::Extrusion] Extrude044
  Base = -> Sketch048
  Dir = (0,0,1)
  DirMode = 2
  FaceMakerClass = Part::FaceMakerBullseye
  LengthFwd = 6.2
  LengthRev = 0
  Solid = true
  Symmetric = false
FEATURE [Part::Fillet] Fillet039
  Base = -> Extrude044
  Edges = 1 edges r=3.09: [Edge7]
FEATURE [Part::Fillet] Fillet040
  Base = -> Fillet039
  Edges = 1 edges r=3.09: [Edge8]
FEATURE [Part::Fillet] Fillet041
  Base = -> Fillet040
  Edges = 1 edges r=3.09: [Edge17]
FEATURE [Part::Fillet] Fillet042  label="removeFromMainToMakeUSBCableHole"
  Base = -> Fillet041
  Edges = 1 edges r=3.09: [Edge10]
  Placement = pos=(-111.4,30,10.9) rot=(0,1,0;1.5708rad)
FEATURE [Part::Cylinder] Cylinder
  Angle = 360
  AttacherType = Attacher::AttachEngine3D
  Height = 17.6
  Placement = pos=(-116.86,-14.05,2.4) rot=(0,0,1;0rad)
  Radius = 8.4
FEATURE [Part::Box] Box080  label="Cube080"
  AttacherType = Attacher::AttachEngine3D
  Height = 20
  Length = 6
  Placement = pos=(-120.65,-16.05,2.4) rot=(0,0,-1;0.349066rad)
  Width = 13.85
FEATURE [Part::Cylinder] Cylinder005
  Angle = 360
  AttacherType = Attacher::AttachEngine3D
  Height = 20
  Placement = pos=(-116.86,-14.05,30) rot=(0,0,1;0rad)
  Radius = 11.06
FEATURE [Part::Box] Box081  label="Cube081"
  AttacherType = Attacher::AttachEngine3D
  Height = 20
  Length = 10
  Placement = pos=(-115.9,-3.3,30) rot=(0,0,-1;0.314159rad)
  Width = 10
FEATURE [App::MeasureDistance] Distance001  label="Distance: 2.40 mm"
  Distance = 2.4
  P1 = (-129.5,-19.3,2.4)
  P2 = (-129.5,-19.3,0)
FEATURE [Part::MultiFuse] Fusion047
  Shapes = -> [Box080,Cylinder]
FEATURE [Part::Cylinder] Cylinder006
  Angle = 360
  AttacherType = Attacher::AttachEngine3D
  Height = 10
  Placement = pos=(-112,-13.1,17) rot=(0,1,0;1.5708rad)
  Radius = 4.4
FEATURE [Part::MultiFuse] Fusion048  label="removeFromMainToCreateHoleForUSBCablePillar"
  Shapes = -> [Fusion047,Cylinder006]
FEATURE [Part::Extrusion] Extrude046
  Base = -> Sketch047
  Dir = (0,0,1)
  DirMode = 2
  FaceMakerClass = Part::FaceMakerBullseye
  LengthFwd = 8
  LengthRev = 0
  Solid = true
  Symmetric = false
FEATURE [App::MeasureDistance] Distance002  label="Distance: 12.20 mm"
  Distance = 12.2
  P1 = (32.7,-36,8)
  P2 = (20.5,-36,8)
FEATURE [Part::Fillet] Fillet
  Base = -> Extrude046
  Edges = 1 edges r=3.9: [Edge12]
FEATURE [Part::Fillet] Fillet048
  Base = -> Fillet
  Edges = 1 edges r=3.9: [Edge8]
FEATURE [Part::Fillet] Fillet049
  Base = -> Fillet048
  Edges = 1 edges r=3.9: [Edge17]
FEATURE [Part::Fillet] Fillet050
  Base = -> Fillet049
  Edges = 1 edges r=3.9: [Edge11]
  Placement = pos=(-55,0,8.3) rot=(1,0,0;0.191986rad)
FEATURE [Part::MultiFuse] Fusion049
  Shapes = -> [Fillet031,Fillet036,Fillet037]
FEATURE [Part::Cut] Cut027
  Base = -> Cylinder005
  Placement = pos=(0,0,-30) rot=(0,0,1;0rad)
  Tool = -> Box081
FEATURE [Sketcher::SketchObject] Sketch049
  FullyConstrained = true
  sketch-geometry (4):
    g0: LineSegment StartX=-5.1 StartY=-34.18 StartZ=0 EndX=5.1 EndY=-34.18 EndZ=0
    g1: LineSegment StartX=-5.1 StartY=-3.93167e-07 StartZ=0 EndX=-5.1 EndY=-34.18 EndZ=0
    g2: LineSegment StartX=5.1 StartY=-34.18 StartZ=0 EndX=5.1 EndY=-3.93167e-07 EndZ=0
    g3: LineSegment StartX=-5.1 StartY=-3.93167e-07 StartZ=0 EndX=5.1 EndY=-3.93167e-07 EndZ=0
  constraints (10):
    c: Horizontal(g0)
    c: Block(g0)
    c: Coincident(g1,g0)
    c: Vertical(g1)
    c: Coincident(g2,g0)
    c: Vertical(g2)
    c: Coincident(g3,g1)
    c: Coincident(g3,g2)
    c: Horizontal(g3)
    c: Block(g3)
FEATURE [Part::Extrusion] Extrude047
  Base = -> Sketch049
  Dir = (0,0,1)
  DirMode = 2
  FaceMakerClass = Part::FaceMakerBullseye
  LengthFwd = 6.2
  LengthRev = 0
  Solid = true
  Symmetric = false
FEATURE [Part::Fillet] Fillet054
  Base = -> Extrude047
  Edges = 1 edges r=3.09: [Edge7]
FEATURE [Part::Fillet] Fillet051
  Base = -> Fillet054
  Edges = 1 edges r=3.09: [Edge8]
FEATURE [Part::Fillet] Fillet052
  Base = -> Fillet051
  Edges = 1 edges r=3.09: [Edge17]
FEATURE [Part::Fillet] Fillet053  label="removeFromMainToMakeUSBCableHole001"
  Base = -> Fillet052
  Edges = 1 edges r=3.09: [Edge10]
  Placement = pos=(-111.4,30,14.9) rot=(0,1,0;1.5708rad)
FEATURE [Sketcher::SketchObject] Sketch050
  FullyConstrained = true
  sketch-geometry (4):
    g0: LineSegment StartX=-5.1 StartY=-34.18 StartZ=0 EndX=5.1 EndY=-34.18 EndZ=0
    g1: LineSegment StartX=-5.1 StartY=-3.93167e-07 StartZ=0 EndX=-5.1 EndY=-34.18 EndZ=0
    g2: LineSegment StartX=5.1 StartY=-34.18 StartZ=0 EndX=5.1 EndY=-3.93167e-07 EndZ=0
    g3: LineSegment StartX=-5.1 StartY=-3.93167e-07 StartZ=0 EndX=5.1 EndY=-3.93167e-07 EndZ=0
  constraints (10):
    c: Horizontal(g0)
    c: Block(g0)
    c: Coincident(g1,g0)
    c: Vertical(g1)
    c: Coincident(g2,g0)
    c: Vertical(g2)
    c: Coincident(g3,g1)
    c: Coincident(g3,g2)
    c: Horizontal(g3)
    c: Block(g3)
FEATURE [Part::Extrusion] Extrude048
  Base = -> Sketch050
  Dir = (0,0,1)
  DirMode = 2
  FaceMakerClass = Part::FaceMakerBullseye
  LengthFwd = 6.2
  LengthRev = 0
  Solid = true
  Symmetric = false
FEATURE [Part::Fillet] Fillet058
  Base = -> Extrude048
  Edges = 1 edges r=3.09: [Edge7]
FEATURE [Part::Fillet] Fillet056
  Base = -> Fillet058
  Edges = 1 edges r=3.09: [Edge8]
FEATURE [Part::Fillet] Fillet055
  Base = -> Fillet056
  Edges = 1 edges r=3.09: [Edge17]
FEATURE [Part::Fillet] Fillet057  label="removeFromMainToMakeUSBCableHole002"
  Base = -> Fillet055
  Edges = 1 edges r=3.09: [Edge10]
  Placement = pos=(-111.4,30,18.4) rot=(0,1,0;1.5708rad)
FEATURE [Part::MultiFuse] Fusion050  label="removeFusion050"
  Shapes = -> [Fillet057,Fillet053,Fillet042]
FEATURE [Part::Box] Box082  label="Cube082"
  AttacherType = Attacher::AttachEngine3D
  Height = 3
  Length = 3
  Placement = pos=(-20,-23.5,17) rot=(0,0,1;0rad)
  Width = 23
FEATURE [Part::Box] Box083  label="Cube083"
  AttacherType = Attacher::AttachEngine3D
  Height = 3
  Length = 3
  Placement = pos=(-40,-23.5,17) rot=(0,0,1;0rad)
  Width = 23
FEATURE [Part::Box] Box086  label="Cube086"
  AttacherType = Attacher::AttachEngine3D
  Height = 8
  Length = 28
  Placement = pos=(-132,-26,0) rot=(0,0,1;0rad)
  Width = 23
FEATURE [Part::Box] Box087  label="Cube087"
  AttacherType = Attacher::AttachEngine3D
  Height = 8
  Length = 12
  Placement = pos=(-98,-26,0) rot=(0,0,1;0rad)
  Width = 23
FEATURE [Part::Box] Box088  label="Cube088"
  AttacherType = Attacher::AttachEngine3D
  Height = 8
  Length = 12
  Placement = pos=(-108,-10,0) rot=(0,0,1;0rad)
  Width = 8
FEATURE [Part::MultiFuse] Fusion051  label="extraStrengthFusion051"
  Shapes = -> [Box087,Box088,Box086]
FEATURE [Part::Fillet] Fillet059
  Base = -> Fusion051
  Edges = 1 edges r=4: [Edge8]
FEATURE [Part::MultiFuse] Fusion052  label="main"
  Shapes = -> [Box083,Box082,Cut017,Extrude001,Fillet059,Revolve]
FEATURE [Part::Cut] Cut028
  Base = -> Fusion052
  Tool = -> Fusion050
FEATURE [Part::Fillet] Fillet060
  Base = -> Cut028
  Edges = 1 edges r=2: [Edge287]
FEATURE [Part::Cut] Cut029
  Base = -> Fillet060
  Tool = -> Fillet050
FEATURE [Part::Cut] Cut030
  Base = -> Cut029
  Tool = -> Fusion049
FEATURE [Part::Cut] Cut031  label="mainCut031"
  Base = -> Cut030
  Tool = -> Fusion037
FEATURE [App::MeasureDistance] Distance003  label="Distance: 69.20 mm"
  Distance = 69.2
  P1 = (-2.5,-29.6975,8.49911)
  P2 = (-71.7,-29.6975,8.49911)
FEATURE [App::MeasureDistance] Distance004  label="Distance: 10.00 mm"
  Distance = 10
  P1 = (-56.7,-29.6975,8.49911)
  P2 = (-46.7,-29.6975,8.49911)
FEATURE [Sketcher::SketchObject] Sketch051
  FullyConstrained = true
  MapMode = 4
  Placement = pos=(0,0,0) rot=(0.57735,0.57735,0.57735;2.0944rad)
  sketch-geometry (14):
    g0: LineSegment StartX=6.08745 StartY=-4.11588 StartZ=0 EndX=6.08745 EndY=-2.11589 EndZ=0
    g1: LineSegment StartX=8.08745 StartY=1.38411 StartZ=0 EndX=8.08745 EndY=-1.11589 EndZ=0
    g2: ArcOfCircle CenterX=7.08745 CenterY=-1.11589 CenterZ=0 NormalX=0 NormalY=0 NormalZ=1 AngleXU=0 Radius=1 StartAngle=4.71239 EndAngle=6.28319
    g3: LineSegment StartX=6.08745 StartY=-2.11589 StartZ=0 EndX=7.08745 EndY=-2.11589 EndZ=0
    g4: LineSegment StartX=6.08745 StartY=-4.11588 StartZ=0 EndX=7.08745 EndY=-4.11588 EndZ=0
    g5: ArcOfCircle CenterX=7.08745 CenterY=-1.11589 CenterZ=0 NormalX=0 NormalY=0 NormalZ=1 AngleXU=0 Radius=3 StartAngle=4.71239 EndAngle=6.28319
    g6: ArcOfCircle CenterX=7.08745 CenterY=1.38411 CenterZ=0 NormalX=0 NormalY=0 NormalZ=1 AngleXU=0 Radius=1 StartAngle=5.35e-14 EndAngle=1.5708
    g7: LineSegment StartX=10.0875 StartY=-1.11588 StartZ=0 EndX=10.0875 EndY=1.38411 EndZ=0
    g8: ArcOfCircle CenterX=7.08745 CenterY=1.38411 CenterZ=0 NormalX=0 NormalY=0 NormalZ=1 AngleXU=0 Radius=3 StartAngle=3.57e-14 EndAngle=1.5708
    g9: ArcOfCircle CenterX=4.58745 CenterY=1.38412 CenterZ=0 NormalX=0 NormalY=0 NormalZ=1 AngleXU=0 Radius=1 StartAngle=1.57081 EndAngle=3.14159
    g10: LineSegment StartX=4.58744 StartY=2.38411 StartZ=0 EndX=7.08745 EndY=2.38411 EndZ=0
    g11: LineSegment StartX=4.58745 StartY=4.38411 StartZ=0 EndX=7.08745 EndY=4.38411 EndZ=0
    g12: ArcOfCircle CenterX=4.58745 CenterY=5.38411 CenterZ=0 NormalX=0 NormalY=0 NormalZ=1 AngleXU=0 Radius=1 StartAngle=3.14159 EndAngle=4.71239
    g13: LineSegment StartX=3.58745 StartY=5.38411 StartZ=0 EndX=3.58745 EndY=1.38411 EndZ=0
  constraints (33):
    c: Vertical(g0)
    c: Block(g0)
    c: Block(g1)
    c: Coincident(g2,g1)
    c: Coincident(g3,g0)
    c: Coincident(g3,g2)
    c: Horizontal(g3)
    c: Block(g2)
    c: Coincident(g4,g0)
    c: Horizontal(g4)
    c: Coincident(g5,g2)
    c: Block(g5)
    c: Block(g4)
    c: Coincident(g6,g1)
    c: Block(g6)
    c: Coincident(g7,g5)
    c: Vertical(g7)
    c: Coincident(g8,g6)
    c: Block(g8)
    c: Block(g7)
    c: Coincident(g10,g9)
    c: Coincident(g10,g6)
    c: Horizontal(g10)
    c: Block(g10)
    c: Block(g9)
    c: Coincident(g11,g8)
    c: Horizontal(g11)
    c: Block(g12)
    c: Block(g11)
    c: Coincident(g13,g12)
    c: Coincident(g13,g9)
    c: Vertical(g13)
    c: Tangent(g13,g9)
FEATURE [Part::Extrusion] Extrude049
  Base = -> Sketch051
  Dir = (1,0,0)
  DirMode = 2
  FaceMakerClass = Part::FaceMakerBullseye
  LengthFwd = 10
  LengthRev = 0
  Placement = pos=(-34.55,-22.61,4.115) rot=(0,0,1;3.14159rad)
  Solid = true
  Symmetric = false
FEATURE [Part::Box] Box089  label="Cube089"
  AttacherType = Attacher::AttachEngine3D
  Height = 2
  Length = 2
  Placement = pos=(-87.7,-21.3,0) rot=(0,0,1;0rad)
  Width = 2
FEATURE [Part::Box] Box090  label="Cube090"
  AttacherType = Attacher::AttachEngine3D
  Height = 2
  Length = 2
  Placement = pos=(-85.7,-21.3,0) rot=(0,0,1;0rad)
  Width = 2
FEATURE [Part::MultiFuse] Fusion053
  Placement = pos=(55.15,-6.9,0) rot=(0,0,1;0rad)
  Shapes = -> [Box090,Box089]
FEATURE [Part::Box] Box091  label="Cube091"
  AttacherType = Attacher::AttachEngine3D
  Height = 2
  Length = 2
  Placement = pos=(-87.7,-21.3,0) rot=(0,0,1;0rad)
  Width = 2
FEATURE [Part::Box] Box092  label="Cube092"
  AttacherType = Attacher::AttachEngine3D
  Height = 2
  Length = 2
  Placement = pos=(-85.7,-21.3,0) rot=(0,0,1;0rad)
  Width = 2
FEATURE [Part::MultiFuse] Fusion054
  Placement = pos=(79.2,-6.9,0) rot=(0,0,1;0rad)
  Shapes = -> [Box092,Box091]
FEATURE [Part::Box] Box093  label="Cube093"
  AttacherType = Attacher::AttachEngine3D
  Height = 2
  Length = 2
  Placement = pos=(-87.7,-21.3,0) rot=(0,0,1;0rad)
  Width = 2
FEATURE [Part::Box] Box094  label="Cube094"
  AttacherType = Attacher::AttachEngine3D
  Height = 2
  Length = 2
  Placement = pos=(-85.7,-21.3,0) rot=(0,0,1;0rad)
  Width = 2
FEATURE [Part::MultiFuse] Fusion055
  Placement = pos=(97.2,-6.9,0) rot=(0,0,1;0rad)
  Shapes = -> [Box094,Box093]
FEATURE [Part::Box] Box095  label="Cube095"
  AttacherType = Attacher::AttachEngine3D
  Height = 2
  Length = 2
  Placement = pos=(-87.7,-21.3,0) rot=(0,0,1;0rad)
  Width = 2
FEATURE [Part::Box] Box096  label="Cube096"
  AttacherType = Attacher::AttachEngine3D
  Height = 2
  Length = 2
  Placement = pos=(-85.7,-21.3,0) rot=(0,0,1;0rad)
  Width = 2
FEATURE [Part::MultiFuse] Fusion056
  Placement = pos=(18,-6.9,0) rot=(0,0,1;0rad)
  Shapes = -> [Box096,Box095]
